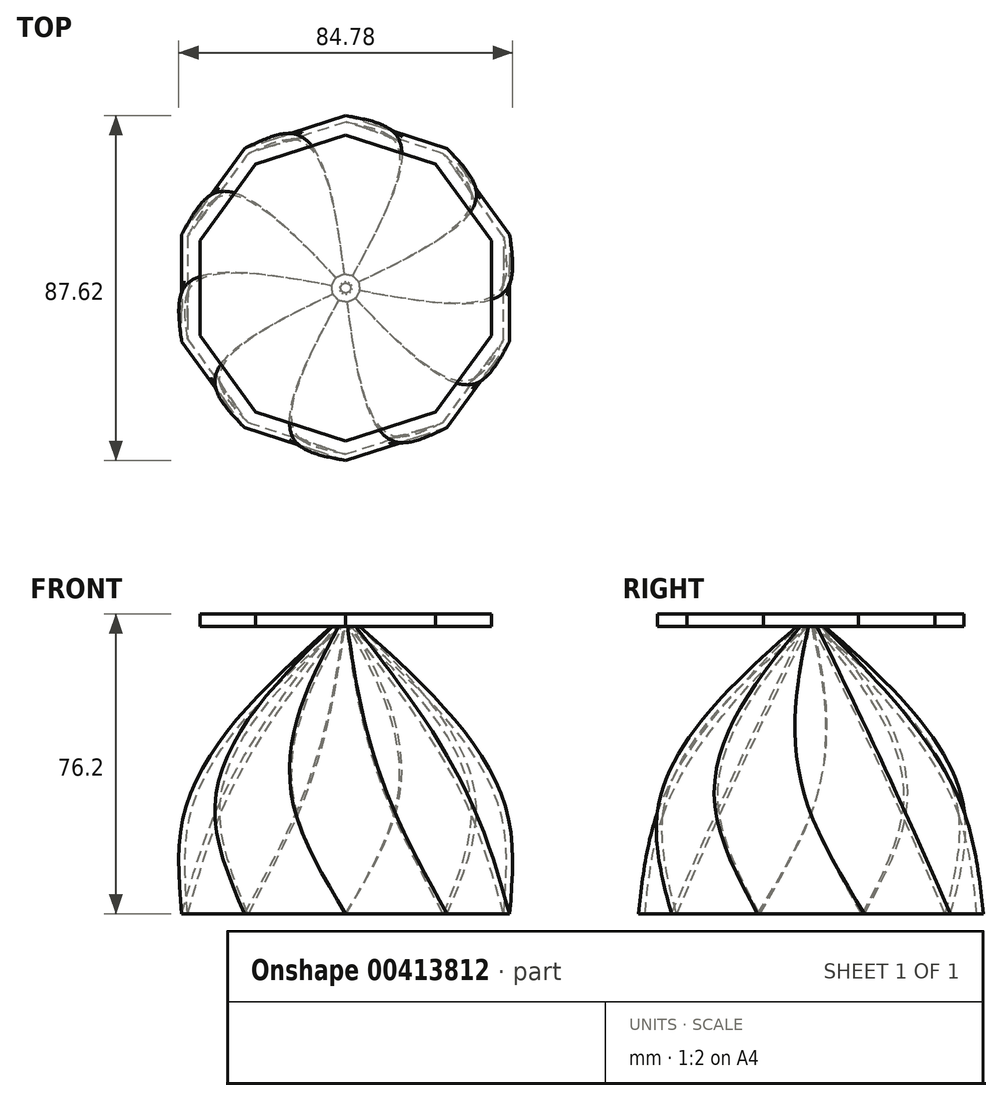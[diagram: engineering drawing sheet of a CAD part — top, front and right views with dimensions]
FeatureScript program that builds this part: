
annotation { "Feature Type Name" : "Feature", "Feature Type Description" : "" }
export const myFeature = defineFeature(function(context is Context, id is Id, definition is map)
    precondition{}
    {
        {
            var Q0;
            Q0=qCreatedBy(makeId("Top.planeOp"),FACE);
            var sketch = newSketch(context, id + "F0", { "sketchPlane" : qUnion([Q0])});
            skCircle(sketch, "E0.cCircle", {"center": v(0, 0) * mm, "radius": 41.67 * mm, "construction": true});
            skLineSegment(sketch, "E0.0", {"start": v(-41.67, -13.54) * mm, "end": v(-41.67, 13.54) * mm});
            skLineSegment(sketch, "E0.1", {"start": v(-41.67, 13.54) * mm, "end": v(-25.75, 35.44) * mm});
            skLineSegment(sketch, "E0.2", {"start": v(-25.75, 35.44) * mm, "end": v(0, 43.8) * mm});
            skLineSegment(sketch, "E0.3", {"start": v(0, 43.8) * mm, "end": v(25.75, 35.44) * mm});
            skLineSegment(sketch, "E0.4", {"start": v(25.75, 35.44) * mm, "end": v(41.67, 13.54) * mm});
            skLineSegment(sketch, "E0.5", {"start": v(41.67, 13.54) * mm, "end": v(41.67, -13.54) * mm});
            skLineSegment(sketch, "E0.6", {"start": v(41.67, -13.54) * mm, "end": v(25.75, -35.44) * mm});
            skLineSegment(sketch, "E0.7", {"start": v(25.75, -35.44) * mm, "end": v(0, -43.8) * mm});
            skLineSegment(sketch, "E0.8", {"start": v(0, -43.8) * mm, "end": v(-25.75, -35.44) * mm});
            skLineSegment(sketch, "E0.9", {"start": v(-25.75, -35.44) * mm, "end": v(-41.67, -13.54) * mm});
            skPoint(sketch, "E0.0.midPoint", {"position": v(-41.67, 0) * mm});
            skSolve(sketch);
        }
        {
            var Q0;
            Q0=qCreatedBy(makeId("Top.planeOp"),FACE);
            cPlane(context, id + "F1", {"entities" : qUnion([Q0]), "cplaneType" : CPlaneType.OFFSET, "offset" : 25.4 * mm, "width" : 152.4 * mm, "height" : 152.4 * mm});
        }
        {
            var Q0;
            Q0=qCreatedBy(id+"F1.planeOp",FACE);
            var sketch = newSketch(context, id + "F2", { "sketchPlane" : qUnion([Q0])});
            skCircle(sketch, "E1.cCircle", {"center": v(0, 0) * mm, "radius": 39.07 * mm, "construction": true});
            skLineSegment(sketch, "E1.0", {"start": v(-12.7, 39.07) * mm, "end": v(12.7, 39.07) * mm});
            skLineSegment(sketch, "E1.1", {"start": v(12.7, 39.07) * mm, "end": v(33.24, 24.15) * mm});
            skLineSegment(sketch, "E1.2", {"start": v(33.24, 24.15) * mm, "end": v(41.08, 0) * mm});
            skLineSegment(sketch, "E1.3", {"start": v(41.08, 0) * mm, "end": v(33.24, -24.15) * mm});
            skLineSegment(sketch, "E1.4", {"start": v(33.24, -24.15) * mm, "end": v(12.7, -39.07) * mm});
            skLineSegment(sketch, "E1.5", {"start": v(12.7, -39.07) * mm, "end": v(-12.7, -39.07) * mm});
            skLineSegment(sketch, "E1.6", {"start": v(-12.7, -39.07) * mm, "end": v(-33.24, -24.15) * mm});
            skLineSegment(sketch, "E1.7", {"start": v(-33.24, -24.15) * mm, "end": v(-41.08, 0) * mm});
            skLineSegment(sketch, "E1.8", {"start": v(-41.08, 0) * mm, "end": v(-33.24, 24.15) * mm});
            skLineSegment(sketch, "E1.9", {"start": v(-33.24, 24.15) * mm, "end": v(-12.7, 39.07) * mm});
            skPoint(sketch, "E1.0.midPoint", {"position": v(0, 39.07) * mm});
            skSolve(sketch);
        }
        {
            var Q0;
            Q0=qCreatedBy(id+"F1.planeOp",FACE);
            cPlane(context, id + "F3", {"entities" : qUnion([Q0]), "cplaneType" : CPlaneType.OFFSET, "offset" : 50.8 * mm, "width" : 152.4 * mm, "height" : 152.4 * mm});
        }
        {
            var Q0;
            Q0=qCreatedBy(id+"F3.planeOp",FACE);
            var sketch = newSketch(context, id + "F4", { "sketchPlane" : qUnion([Q0])});
            skCircle(sketch, "E2.cCircle", {"center": v(0, 0) * mm, "radius": 37.02 * mm, "construction": true});
            skLineSegment(sketch, "E2.0", {"start": v(-37.02, -12.03) * mm, "end": v(-37.02, 12.03) * mm});
            skLineSegment(sketch, "E2.1", {"start": v(-37.02, 12.03) * mm, "end": v(-22.88, 31.5) * mm});
            skLineSegment(sketch, "E2.2", {"start": v(-22.88, 31.5) * mm, "end": v(0, 38.92) * mm});
            skLineSegment(sketch, "E2.3", {"start": v(0, 38.92) * mm, "end": v(22.88, 31.5) * mm});
            skLineSegment(sketch, "E2.4", {"start": v(22.88, 31.5) * mm, "end": v(37.02, 12.03) * mm});
            skLineSegment(sketch, "E2.5", {"start": v(37.02, 12.03) * mm, "end": v(37.02, -12.03) * mm});
            skLineSegment(sketch, "E2.6", {"start": v(37.02, -12.03) * mm, "end": v(22.88, -31.5) * mm});
            skLineSegment(sketch, "E2.7", {"start": v(22.88, -31.5) * mm, "end": v(0, -38.92) * mm});
            skLineSegment(sketch, "E2.8", {"start": v(0, -38.92) * mm, "end": v(-22.88, -31.5) * mm});
            skLineSegment(sketch, "E2.9", {"start": v(-22.88, -31.5) * mm, "end": v(-37.02, -12.03) * mm});
            skPoint(sketch, "E2.0.midPoint", {"position": v(-37.02, 0) * mm});
            skSolve(sketch);
        }
        {
            var Q0;
            Q0=makeQuery(id+"F0.imprint","IMPRINT",FACE,{"disambiguationData":[TD([[makeQuery(id+"F0.imprint","IMPRINT",EDGE,{"derivedFrom":sQuery(id+"F0.wireOp",EDGE,"E0.0")}),-1.0]])]});
            var Q1;
            Q1=makeQuery(id+"F2.imprint","IMPRINT",FACE,{"disambiguationData":[TD([[makeQuery(id+"F2.imprint","IMPRINT",EDGE,{"derivedFrom":sQuery(id+"F2.wireOp",EDGE,"E1.0")}),-1.0]])]});
            var Q2;
            Q2=sQuery(id+"F4.wireOp",VERTEX,"E2.cCircle.center");
            loft(context, id + "F5", {"sheetProfilesArray" : [{ "sheetProfileEntities" : qUnion([Q0]) }, { "sheetProfileEntities" : qUnion([Q1]) }, { "sheetProfileEntities" : qUnion([Q2]) }]});
        }
        {
            var Q0;
            Q0=makeQuery(id+"F5.opLoft","CAP_FACE",FACE,{"disambiguationData":[OSD([makeQuery(id+"F0.imprint","IMPRINT",FACE,{"disambiguationData":[TD([[makeQuery(id+"F0.imprint","IMPRINT",EDGE,{"derivedFrom":sQuery(id+"F0.wireOp",EDGE,"E0.0")}),-1.0]])]})])],"isStart":true});
            shell(context, id + "F6", {"entities" : qUnion([Q0]), "thickness" : 1.5 * mm});
        }
        {
            var Q0;
            Q0 = qSketchRegion(id + "F4", true);
            extrude(context, id + "F7", {"entities" : qUnion([Q0]), "operationType" : NewBodyOperationType.ADD, "oppositeDirection" : true, "depth" : 3.17 * mm});
        }
    });
